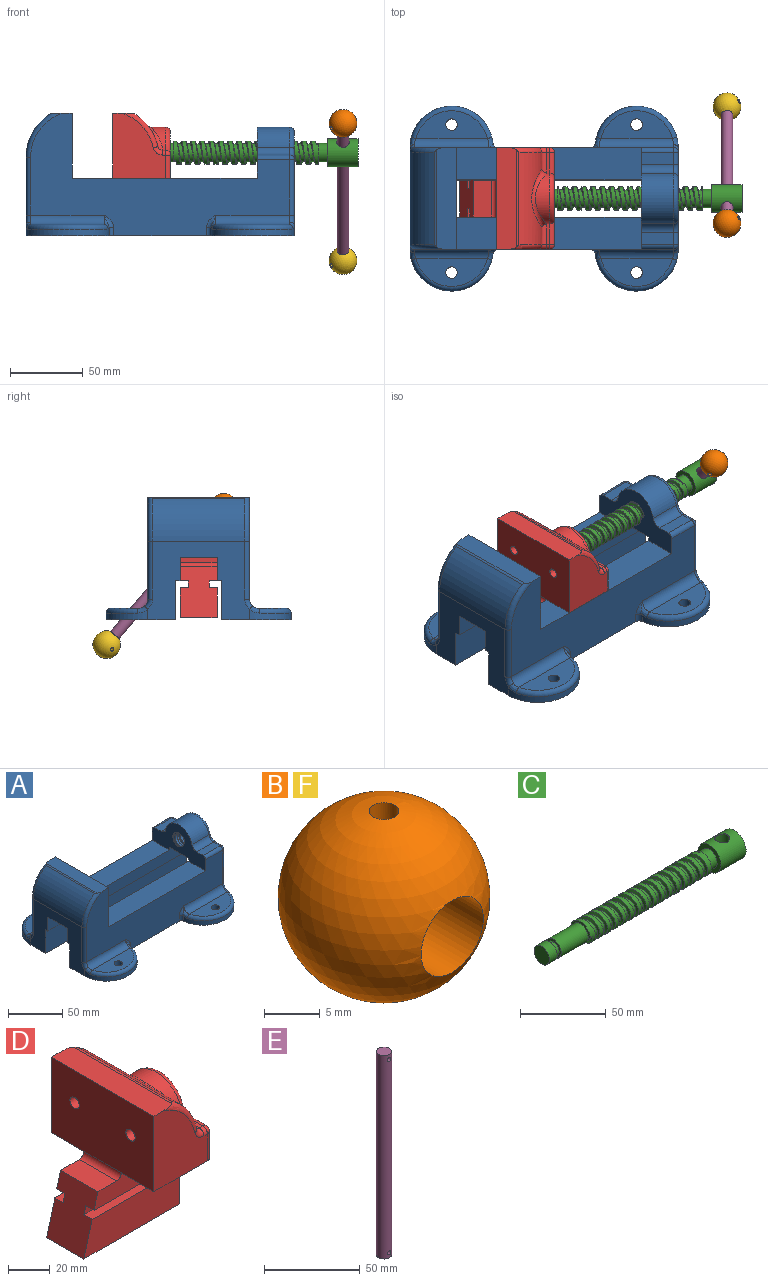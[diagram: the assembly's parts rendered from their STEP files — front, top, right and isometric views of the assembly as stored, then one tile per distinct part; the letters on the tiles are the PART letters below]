
ASSEMBLY  parts=6 mates=6
PART A: 90 faces, bbox 191.8x135.1x93.3 mm
  f0: plane 69.98x35.06mm, normal (-1,0,0), area 1390.7mm2, adj f1,f4,f6,f7,f9,f25,f26,f27
  f1: cylinder r=6.39mm len=25.4mm, axis (1,0,0), area 430.9mm2, adj f0,f5,f86,f88,f89
  f2: plane 184.15x47.6mm, normal (0,0,-1), area 5973.6mm2, adj f3,f5,f6,f11,f12,f14,f15,f29
  f3: plane 69.85x53.98mm, normal (-1,0,0), area 2224.7mm2, adj f2,f10,f11,f17,f24,f28,f29,f30
  f4: plane 127x22.2mm, normal (0,0,1), area 2819.3mm2, adj f0,f7,f23,f35
  f5: plane 71.56x69.98mm, normal (1,0,0), area 2448.5mm2, adj f1,f2,f10,f14,f20,f28,f29,f30
  f6: plane 181.19x87.52mm, normal (0,1,0), area 6838.3mm2, adj f0,f2,f8,f9,f23,f42,f45,f51
  f7: plane 181.19x87.52mm, normal (0,-1,0), area 6838.3mm2, adj f0,f4,f8,f10,f23,f43,f44,f46
  f8: plane 70.71x14.43mm, normal (0,0,1), area 942.4mm2, adj f6,f7,f23,f81,f83,f85
  f9: plane 127x22.2mm, normal (0,0,1), area 2819.3mm2, adj f0,f6,f23,f32
  f10: plane 184.15x47.6mm, normal (0,0,-1), area 5973.6mm2, adj f3,f5,f7,f17,f18,f20,f21,f28
  f11: cylinder r=28.57mm len=57.01mm, axis (0,0,-1), area 423.3mm2, adj f2,f3,f69,f71,f73,f75
  f12: cylinder r=3.96mm len=7.93mm, axis (0,0,-1), area 197.3mm2, adj f2,f13
  f13: plane 49.19x19.05mm, normal (0,0,1), area 644.9mm2, adj f12,f42,f73
  f14: cylinder r=28.57mm len=57.01mm, axis (0,0,-1), area 423.3mm2, adj f2,f5,f51,f56,f58,f60
  f15: cylinder r=3.96mm len=7.93mm, axis (0,0,-1), area 197.3mm2, adj f2,f16
  f16: plane 49.19x19.05mm, normal (0,0,1), area 644.9mm2, adj f15,f45,f58
  f17: cylinder r=28.57mm len=57.01mm, axis (0,0,-1), area 423.3mm2, adj f3,f10,f72,f76,f78,f80
  f18: cylinder r=3.96mm len=7.93mm, axis (0,0,-1), area 197.3mm2, adj f10,f19
  f19: plane 49.19x19.05mm, normal (0,0,1), area 644.9mm2, adj f18,f43,f78
  f20: cylinder r=28.57mm len=57.01mm, axis (0,0,-1), area 423.3mm2, adj f5,f10,f46,f48,f49,f50
  f21: cylinder r=3.96mm len=7.93mm, axis (0,0,-1), area 197.3mm2, adj f10,f22
  f22: plane 49.19x19.05mm, normal (0,0,1), area 644.9mm2, adj f21,f44,f49
  f23: plane 69.85x44.45mm, normal (1,0,0), area 2960.4mm2, adj f4,f6,f7,f8,f9,f32,f34,f35
  f24: cylinder r=34.92mm len=63.5mm, axis (0,-1,0), area 2251.5mm2, adj f3,f81,f83,f85
  f25: cylinder r=17.45mm len=34.2mm, axis (1,0,0), area 1062.5mm2, adj f0,f40,f41,f63
  f26: plane 22.23x8.43mm, normal (0,0,1), area 187.3mm2, adj f0,f41,f64,f68
  f27: plane 22.23x8.43mm, normal (0,0,1), area 187.3mm2, adj f0,f40,f55,f59
  f28: plane 184.15x26.97mm, normal (0,1,0), area 4967.4mm2, adj f3,f5,f10,f31
  f29: plane 184.15x26.97mm, normal (0,-1,0), area 4967.4mm2, adj f2,f3,f5,f30
  f30: plane 184.15x3.18mm, normal (0,0,-1), area 584.7mm2, adj f3,f5,f29,f32
  f31: plane 184.15x3.18mm, normal (0,0,-1), area 584.7mm2, adj f3,f5,f28,f35
  f32: plane 184.15x15.89mm, normal (0,-1,0), area 2520.9mm2, adj f0,f3,f5,f9,f23,f30,f33,f34
  f33: plane 25.45x25.4mm, normal (0,0,-1), area 646.5mm2, adj f0,f5,f32,f35
  f34: plane 31.75x25.45mm, normal (0,0,-1), area 808.1mm2, adj f3,f23,f32,f35
  f35: plane 184.15x15.89mm, normal (0,1,0), area 2520.9mm2, adj f0,f3,f4,f5,f23,f31,f33,f34
  f36: cylinder r=3.17mm len=15.88mm, axis (1,0,0), area 316.7mm2, adj f23,f37
  f37: plane 6.35x6.35mm, normal (1,0,0), area 31.7mm2, adj f36
  f38: cylinder r=3.17mm len=15.88mm, axis (1,0,0), area 316.7mm2, adj f23,f39
  f39: plane 6.35x6.35mm, normal (1,0,0), area 31.7mm2, adj f38
  f40: cylinder r=6.35mm len=22.23mm, axis (1,0,0), area 193.3mm2, adj f0,f25,f27,f61
  f41: cylinder r=6.35mm len=22.23mm, axis (1,0,0), area 193.3mm2, adj f0,f25,f26,f66
  f42: cylinder r=6.35mm len=50.6mm, axis (-1,0,0), area 499.8mm2, adj f6,f13,f71,f75,f77
  f43: cylinder r=6.35mm len=50.6mm, axis (1,0,0), area 499.8mm2, adj f7,f19,f76,f80,f82
  f44: cylinder r=6.35mm len=50.6mm, axis (1,0,0), area 499.8mm2, adj f7,f22,f48,f50,f52
  f45: cylinder r=6.35mm len=50.6mm, axis (-1,0,0), area 499.8mm2, adj f6,f16,f56,f60,f62
  f46: cylinder r=3.17mm len=5.55mm, axis (0,0,-1), area 25.9mm2, adj f7,f10,f20,f47
  f47: bspline ~10.3x6.39mm, area 17.6mm2, adj f7,f46,f48
  f48: bspline ~11.96x10.37mm, area 38.2mm2, adj f20,f44,f47,f49
  f49: torus R=25.4mm, axis (0,0,1), area 360.5mm2, adj f20,f22,f48,f50
  f50: bspline ~9.34x5.4mm, area 29.6mm2, adj f20,f44,f49,f52
  f51: cylinder r=3.17mm len=5.55mm, axis (0,0,-1), area 25.9mm2, adj f2,f6,f14,f53
  f52: torus R=9.53mm, axis (1,0,0), area 31.5mm2, adj f5,f44,f50,f54
  f53: bspline ~10.3x6.39mm, area 15.9mm2, adj f6,f51,f56
  f54: cylinder r=3.17mm len=38.1mm, axis (0,0,1), area 190mm2, adj f5,f7,f52,f57
  f55: cylinder r=3.17mm len=22.23mm, axis (-1,0,0), area 110.8mm2, adj f0,f7,f27,f57
  f56: bspline ~11.96x10.37mm, area 38.2mm2, adj f14,f45,f53,f58
  f57: sphere r=3.17mm, area 15.8mm2, adj f54,f55,f59
  f58: torus R=25.4mm, axis (0,0,1), area 360.5mm2, adj f14,f16,f56,f60
  f59: cylinder r=3.17mm len=8.43mm, axis (0,-1,0), area 42mm2, adj f5,f27,f57,f61
  f60: bspline ~9.34x5.4mm, area 29.6mm2, adj f14,f45,f58,f62
  f61: torus R=9.53mm, axis (1,0,0), area 51.3mm2, adj f5,f40,f59,f63
  f62: torus R=9.53mm, axis (1,0,0), area 31.5mm2, adj f5,f45,f60,f65
  f63: torus R=14.27mm, axis (1,0,0), area 222.7mm2, adj f5,f25,f61,f66
  f64: cylinder r=3.17mm len=22.23mm, axis (-1,0,0), area 110.8mm2, adj f0,f6,f26,f67
  f65: cylinder r=3.17mm len=38.1mm, axis (0,0,-1), area 190mm2, adj f5,f6,f62,f67
  f66: torus R=9.53mm, axis (1,0,0), area 51.3mm2, adj f5,f41,f63,f68
  f67: sphere r=3.17mm, area 10.1mm2, adj f64,f65,f68
  f68: cylinder r=3.17mm len=8.43mm, axis (0,-1,0), area 42mm2, adj f5,f26,f66,f67
  f69: cylinder r=3.17mm len=5.55mm, axis (0,0,-1), area 25.9mm2, adj f2,f6,f11,f70
  f70: bspline ~10.3x6.39mm, area 17.6mm2, adj f6,f69,f71
  f71: bspline ~11.96x10.37mm, area 38.2mm2, adj f11,f42,f70,f73
  f72: cylinder r=3.17mm len=5.55mm, axis (0,0,-1), area 25.9mm2, adj f7,f10,f17,f74
  f73: torus R=25.4mm, axis (0,0,1), area 360.5mm2, adj f11,f13,f71,f75
  f74: bspline ~10.3x6.39mm, area 15.9mm2, adj f7,f72,f76
  f75: bspline ~9.34x5.4mm, area 29.6mm2, adj f11,f42,f73,f77
  f76: bspline ~11.96x10.37mm, area 38.2mm2, adj f17,f43,f74,f78
  f77: torus R=9.53mm, axis (1,0,0), area 31.5mm2, adj f3,f42,f75,f79
  f78: torus R=25.4mm, axis (0,0,1), area 360.5mm2, adj f17,f19,f76,f80
  f79: cylinder r=3.17mm len=39.7mm, axis (0,0,1), area 198mm2, adj f3,f6,f77,f81
  f80: bspline ~9.34x5.4mm, area 29.6mm2, adj f17,f43,f78,f82
  f81: torus R=31.75mm, axis (0,1,0), area 187.9mm2, adj f6,f8,f24,f79,f83
  f82: torus R=9.53mm, axis (1,0,0), area 31.5mm2, adj f3,f43,f80,f84
  f83: cylinder r=3.17mm len=66.71mm, axis (0,-1,0), area 114.8mm2, adj f8,f24,f81,f85
  f84: cylinder r=3.17mm len=39.7mm, axis (0,0,-1), area 198mm2, adj f3,f7,f82,f85
  f85: torus R=31.75mm, axis (0,1,0), area 187.9mm2, adj f7,f8,f24,f83,f84
  f86: plane 1.76x1.55mm, normal (-0.13,-0.01,0.99), area 2.4mm2, adj f0,f1,f87,f89
  f87: cylinder r=7.94mm len=25.4mm, axis (-1,0,0), area 524.5mm2, adj f0,f5,f86,f88,f89
  f88: bspline ~26.93x18.32mm, area 290.1mm2, adj f0,f1,f5,f87
  f89: bspline ~24.81x18.34mm, area 272.9mm2, adj f1,f5,f86,f87
PART B: 5 faces, bbox 19.1x19.1x18.9 mm
  f0: sphere r=9.53mm, area 1077.6mm2, adj f1,f3,f4
  f1: cylinder r=3.96mm len=11.84mm, axis (0,-1,0), area 283.2mm2, adj f0,f2,f3,f4
  f2: plane 7.91x7.91mm, normal (0,-1,0), area 49.2mm2, adj f1
  f3: cylinder r=1.32mm len=5.7mm, axis (0,0,1), area 46.4mm2, adj f0,f1
  f4: cylinder r=1.32mm len=5.7mm, axis (0,0,1), area 46.4mm2, adj f0,f1
PART C: 21 faces, bbox 159.1x19.2x19.2 mm
  f0: cylinder r=9.53mm len=20.63mm, axis (-1,0,0), area 1111.2mm2, adj f18,f19,f20
  f1: plane 16.01x15.91mm, normal (1,0,0), area 53.5mm2, adj f2,f7,f8,f17
  f2: cylinder r=7.94mm len=100mm, axis (-1,0,0), area 3461mm2, adj f1,f3,f4,f6,f7,f8
  f3: plane 16.02x15.87mm, normal (-1,0,0), area 53.5mm2, adj f2,f4,f6,f10
  f4: plane 1.85x1.76mm, normal (0.13,0.01,-0.99), area 2.8mm2, adj f2,f3,f5,f8,f9
  f5: bspline ~103.1x14.08mm, area 1565.3mm2, adj f4,f6,f7,f8,f9,f16
  f6: bspline ~99.96x18.32mm, area 1318.7mm2, adj f2,f3,f5,f7,f9
  f7: plane 1.85x1.76mm, normal (-0.13,0.99,0), area 2.8mm2, adj f1,f2,f5,f6,f16
  f8: bspline ~99.96x18.34mm, area 1312.5mm2, adj f1,f2,f4,f5,f16
  f9: plane 6.27x5.25mm, normal (1,0,0), area 2.1mm2, adj f4,f5,f6,f10
  f10: cylinder r=6.35mm len=22.35mm, axis (1,0,0), area 891.8mm2, adj f3,f9,f11
  f11: plane 12.7x12.7mm, normal (-1,0,0), area 55.4mm2, adj f10,f12
  f12: cylinder r=4.76mm len=9.53mm, axis (1,0,0), area 98.8mm2, adj f11,f15
  f13: cylinder r=6.35mm len=12.7mm, axis (1,0,0), area 253.4mm2, adj f14,f15
  f14: plane 12.7x12.7mm, normal (-1,0,0), area 126.7mm2, adj f13
  f15: plane 12.7x12.7mm, normal (1,0,0), area 55.4mm2, adj f12,f13
  f16: plane 6.3x5.05mm, normal (-1,0,0), area 2.1mm2, adj f5,f7,f8,f17
  f17: cylinder r=6.35mm len=12.7mm, axis (-1,0,0), area 253.4mm2, adj f1,f16,f19
  f18: plane 19.05x19.05mm, normal (1,0,0), area 285mm2, adj f0
  f19: plane 19.05x19.05mm, normal (-1,0,0), area 158.3mm2, adj f0,f17
  f20: cylinder r=4.37mm len=19.05mm, axis (0,0,-1), area 522.6mm2, adj f0
PART D: 48 faces, bbox 65.9x70.7x89.2 mm
  f0: plane 14.38x2.42mm, normal (0,0,1), area 34.6mm2, adj f24,f32,f35,f37,f38
  f1: plane 70.71x14.43mm, normal (0,0,1), area 942.4mm2, adj f2,f4,f23,f36,f39,f42
  f2: plane 44.45x36.5mm, normal (0,1,0), area 1225.7mm2, adj f1,f17,f23,f42,f43,f45,f47
  f3: plane 69.82x63.5mm, normal (1,0,0), area 2160.8mm2, adj f5,f6,f7,f8,f9,f10,f11,f12
  f4: plane 44.45x36.5mm, normal (0,-1,0), area 1225.7mm2, adj f1,f5,f23,f31,f32,f33,f36
  f5: plane 39.68x22.23mm, normal (0,0,-1), area 879.6mm2, adj f3,f4,f6,f23,f31
  f6: plane 58.18x12.83mm, normal (0,-1,0), area 677mm2, adj f3,f5,f7,f20,f21,f22
  f7: plane 58.18x5.59mm, normal (0,0,-1), area 325.1mm2, adj f3,f6,f8,f20
  f8: plane 59.48x4.76mm, normal (0,-1,0), area 280.2mm2, adj f3,f7,f9,f20
  f9: plane 59.48x5.59mm, normal (0,0,1), area 332.4mm2, adj f3,f8,f10,f20
  f10: plane 65.08x20.51mm, normal (0,-1,0), area 1277.4mm2, adj f3,f9,f11,f20
  f11: plane 65.08x25.4mm, normal (0,0,-1), area 1652.9mm2, adj f3,f10,f12,f20
  f12: plane 65.08x20.51mm, normal (0,1,0), area 1277.4mm2, adj f3,f11,f13,f20
  f13: plane 59.48x5.59mm, normal (0,0,1), area 332.4mm2, adj f3,f12,f14,f20
  f14: plane 59.48x4.76mm, normal (0,1,0), area 280.2mm2, adj f3,f13,f15,f20
  f15: plane 58.18x5.59mm, normal (0,0,-1), area 325.1mm2, adj f3,f14,f16,f20
  f16: plane 58.18x12.83mm, normal (0,1,0), area 677mm2, adj f3,f15,f17,f20,f21,f22
  f17: plane 39.68x22.23mm, normal (0,0,-1), area 879.6mm2, adj f2,f3,f16,f23,f43
  f18: cylinder r=34.92mm len=63.5mm, axis (0,-1,0), area 1312.4mm2, adj f35,f36,f38,f39,f41,f42
  f19: plane 14.38x2.42mm, normal (0,0,1), area 34.6mm2, adj f24,f38,f41,f44,f47
  f20: plane 34.93x25.4mm, normal (-0.96,0,0.26), area 864.3mm2, adj f6,f7,f8,f9,f10,f11,f12,f13
  f21: plane 25.4x12.7mm, normal (0,0,1), area 322.6mm2, adj f6,f16,f20,f22
  f22: cylinder r=3.17mm len=25.4mm, axis (0,-1,0), area 126.7mm2, adj f6,f16,f21,f23
  f23: plane 69.85x44.45mm, normal (-1,0,0), area 3041.5mm2, adj f1,f2,f4,f5,f17,f22,f27,f29
  f24: cylinder r=17.45mm len=34.75mm, axis (1,0,0), area 319.6mm2, adj f0,f19,f38,f40
  f25: cylinder r=6.35mm len=30.15mm, axis (1,0,0), area 1202.9mm2, adj f3,f26
  f26: plane 12.7x12.7mm, normal (1,0,0), area 126.7mm2, adj f25
  f27: cylinder r=3.17mm len=15.88mm, axis (-1,0,0), area 316.7mm2, adj f23,f28
  f28: plane 6.35x6.35mm, normal (-1,0,0), area 31.7mm2, adj f27
  f29: cylinder r=3.17mm len=15.88mm, axis (-1,0,0), area 316.7mm2, adj f23,f30
  f30: plane 6.35x6.35mm, normal (-1,0,0), area 31.7mm2, adj f29
  f31: cylinder r=3.17mm len=15.88mm, axis (0,0,1), area 79.2mm2, adj f3,f4,f5,f34
  f32: cylinder r=3.17mm len=3.18mm, axis (1,0,0), area 12mm2, adj f0,f4,f33,f34
  f33: torus R=6.35mm, axis (0,1,0), area 29.4mm2, adj f4,f32,f35,f36
  f34: sphere r=3.17mm, area 15.8mm2, adj f31,f32,f37
  f35: cylinder r=3.17mm len=14.34mm, axis (0,-1,0), area 56.2mm2, adj f0,f18,f33,f38
  f36: torus R=31.75mm, axis (0,1,0), area 152.6mm2, adj f1,f4,f18,f33,f39
  f37: cylinder r=3.17mm len=17.56mm, axis (0,-1,0), area 79.6mm2, adj f0,f3,f34,f40
  f38: bspline ~41.25x18.62mm, area 206.8mm2, adj f0,f18,f19,f24,f35,f41
  f39: cylinder r=3.17mm len=66.71mm, axis (0,-1,0), area 114.8mm2, adj f1,f18,f36,f42
  f40: torus R=14.27mm, axis (1,0,0), area 256.3mm2, adj f3,f24,f37,f44
  f41: cylinder r=3.17mm len=14.34mm, axis (0,-1,0), area 56.2mm2, adj f18,f19,f38,f45
  f42: torus R=31.75mm, axis (0,1,0), area 152.6mm2, adj f1,f2,f18,f39,f45
  f43: cylinder r=3.17mm len=15.88mm, axis (0,0,-1), area 79.2mm2, adj f2,f3,f17,f46
  f44: cylinder r=3.17mm len=17.56mm, axis (0,-1,0), area 79.6mm2, adj f3,f19,f40,f46
  f45: torus R=6.35mm, axis (0,1,0), area 29.4mm2, adj f2,f41,f42,f47
  f46: sphere r=3.17mm, area 10.1mm2, adj f43,f44,f47
  f47: cylinder r=3.17mm len=3.18mm, axis (1,0,0), area 12mm2, adj f2,f19,f45,f46
PART E: 5 faces, bbox 7.9x7.9x130.2 mm
  f0: cylinder r=3.95mm len=130.18mm, axis (0,0,-1), area 3208.4mm2, adj f1,f2,f3,f4
  f1: plane 7.9x7.9mm, normal (0,0,1), area 49mm2, adj f0
  f2: plane 7.9x7.9mm, normal (0,0,-1), area 49mm2, adj f0
  f3: cylinder r=1.35mm len=7.9mm, axis (0,-1,0), area 65.1mm2, adj f0
  f4: cylinder r=1.28mm len=7.9mm, axis (0,-1,0), area 61.9mm2, adj f0
PART F: same geometry as B
PLACE A at identity fixed
PLACE B rot(axis=(0.85,-0.22,-0.48),137.1deg) t=(125.59,-17.16,77.31)mm
PLACE C rot(axis=(1,0,0),40.4deg) t=(8.93,0,57.15)mm
PLACE D t=(-58,2.12,31.01)mm
PLACE E rot(axis=(-0.86,0.48,0.18),144.9deg) t=(125.59,-19.22,79.73)mm
PLACE F rot(axis=(-0.6,0.73,-0.34),75.3deg) t=(125.59,63.11,-16.98)mm
MATE pin_slot C.f0 <-> D.f24  axis (-1,0,0) through (-23.08,0,57.15)mm
MATE pin_slot A.f4 <-> D.f5  axis (0,0,1) through (-60.32,-34.93,39.67)mm
MATE fastened B.f1 <-> E.f0  axis (0,0.65,-0.76) through (125.59,-19.22,79.73)mm
MATE cylindrical A.f87 <-> C.f0  axis (1,0,0) through (66.68,0,57.15)mm
MATE cylindrical E.f0 <-> C.f20  axis (0,-0.65,0.76) through (125.59,22.97,30.17)mm
MATE fastened F.f1 <-> E.f0  axis (0,-0.65,0.76) through (125.59,65.16,-19.39)mm
